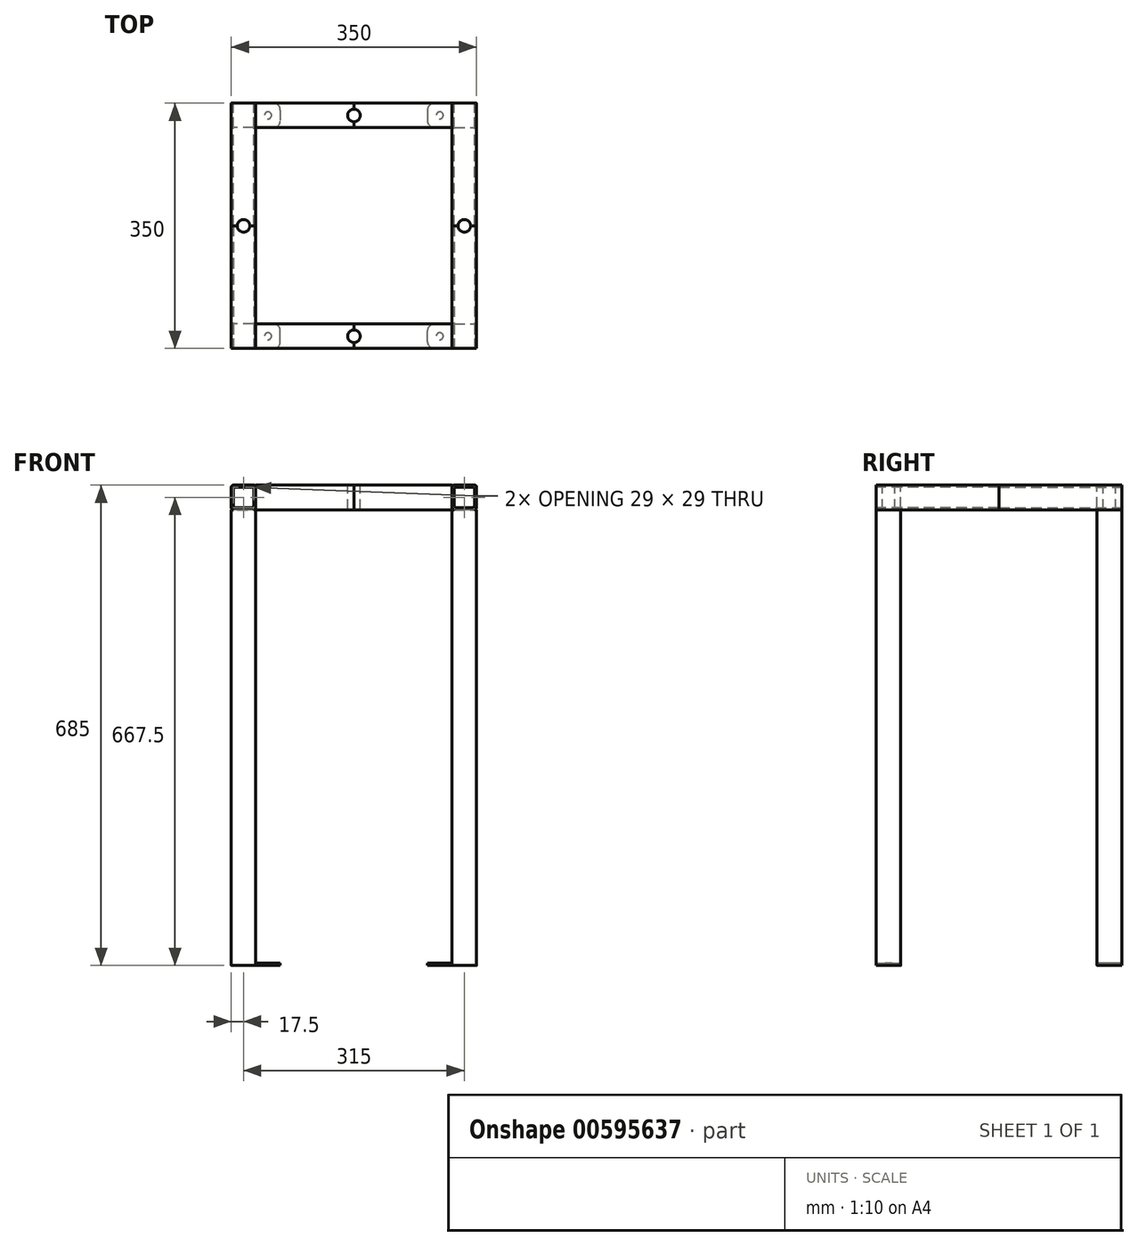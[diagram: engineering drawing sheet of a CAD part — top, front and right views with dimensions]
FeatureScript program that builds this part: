
annotation { "Feature Type Name" : "Feature", "Feature Type Description" : "" }
export const myFeature = defineFeature(function(context is Context, id is Id, definition is map)
    precondition{}
    {
        {
            var Q0;
            Q0=qCreatedBy(makeId("Top.planeOp"),FACE);
            var sketch = newSketch(context, id + "F0", { "sketchPlane" : qUnion([Q0])});
            skLineSegment(sketch, "E0.bottom", {"start": v(3, 0) * mm, "end": v(32, 0) * mm});
            skLineSegment(sketch, "E0.top", {"start": v(3, 35) * mm, "end": v(32, 35) * mm});
            skLineSegment(sketch, "E0.left", {"start": v(0, 3) * mm, "end": v(0, 32) * mm});
            skLineSegment(sketch, "E0.right", {"start": v(35, 3) * mm, "end": v(35, 32) * mm});
            skPoint(sketch, "E1.visualSharp", {"position": v(0, 35) * mm});
            skArc(sketch, "E1.filletArc", {"start": v(3, 35) * mm, "mid": v(0.88, 34.12) * mm, "end": v(0, 32) * mm});
            skPoint(sketch, "E2.visualSharp", {"position": v(35, 35) * mm});
            skArc(sketch, "E2.filletArc", {"start": v(35, 32) * mm, "mid": v(34.12, 34.12) * mm, "end": v(32, 35) * mm});
            skPoint(sketch, "E3.visualSharp", {"position": v(35, 0) * mm});
            skArc(sketch, "E3.filletArc", {"start": v(32, 0) * mm, "mid": v(34.12, 0.88) * mm, "end": v(35, 3) * mm});
            skPoint(sketch, "E4.visualSharp", {"position": v(0, 0) * mm});
            skArc(sketch, "E4.filletArc", {"start": v(0, 3) * mm, "mid": v(0.88, 0.88) * mm, "end": v(3, 0) * mm});
            skSolve(sketch);
        }
        {
            var Q0;
            Q0=makeQuery(id+"F0.imprint","IMPRINT",FACE,{"disambiguationData":[TD([[makeQuery(id+"F0.imprint","IMPRINT",EDGE,{"derivedFrom":sQuery(id+"F0.wireOp",EDGE,"E0.bottom")}),1.0]])]});
            extrude(context, id + "F1", {"entities" : qUnion([Q0]), "depth" : 650 * mm, "offsetDistance" : 25 * mm});
        }
        {
            var Q0;
            Q0=qCreatedBy(makeId("Right.planeOp"),FACE);
            var sketch = newSketch(context, id + "F2", { "sketchPlane" : qUnion([Q0])});
            skLineSegment(sketch, "E5.bottom", {"start": v(0, 0) * mm, "end": v(35, 0) * mm});
            skLineSegment(sketch, "E5.top", {"start": v(0, 3) * mm, "end": v(35, 3) * mm});
            skLineSegment(sketch, "E5.left", {"start": v(0, 0) * mm, "end": v(0, 3) * mm});
            skLineSegment(sketch, "E5.right", {"start": v(35, 0) * mm, "end": v(35, 3) * mm});
            skSolve(sketch);
        }
        {
            var Q0;
            Q0=makeQuery(id+"F2.imprint","IMPRINT",FACE,{"disambiguationData":[TD([[makeQuery(id+"F2.imprint","IMPRINT",EDGE,{"derivedFrom":sQuery(id+"F2.wireOp",EDGE,"E5.bottom")}),1.0]])]});
            extrude(context, id + "F3", {"entities" : qUnion([Q0]), "operationType" : NewBodyOperationType.ADD, "oppositeDirection" : true, "depth" : 35 * mm, "offsetDistance" : 25 * mm});
        }
        {
            var Q0;
            Q0=makeQuery(id+"F3.opExtrude","CAP_EDGE",EDGE,{"disambiguationData":[OSD([sQuery(id+"F2.wireOp",EDGE,"E5.left")])],"isStart":false});
            var Q1;
            Q1=makeQuery(id+"F3.opExtrude","CAP_EDGE",EDGE,{"disambiguationData":[OSD([sQuery(id+"F2.wireOp",EDGE,"E5.right")])],"isStart":false});
            fillet(context, id + "F4", {"entities" : qUnion([Q0, Q1]), "radius" : 10 * mm, "tangentPropagation" : true, "allowEdgeOverflow" : false});
        }
        {
            var Q0;
            Q0=makeQuery(id+"F3.opExtrude","SWEPT_FACE",FACE,{"disambiguationData":[OSD([sQuery(id+"F2.wireOp",EDGE,"E5.top")])]});
            var sketch = newSketch(context, id + "F5", { "sketchPlane" : qUnion([Q0])});
            skPoint(sketch, "E6", {"position": v(-17.5, 17.5) * mm});
            skPoint(sketch, "E6.positionSnap0", {"position": v(-35, 17.5) * mm});
            skSolve(sketch);
        }
        {
            var Q0;
            Q0=sQuery(id+"F5.wireOp",VERTEX,"E6");
            var Q1;
            Q1=makeQuery(id+"F1.opExtrude","SWEPT_BODY",BODY,{"disambiguationData":[OSD([sQuery(id+"F0.wireOp",EDGE,"E0.bottom"),sQuery(id+"F0.wireOp",EDGE,"E0.top"),sQuery(id+"F0.wireOp",EDGE,"E0.left"),sQuery(id+"F0.wireOp",EDGE,"E0.right"),sQuery(id+"F0.wireOp",EDGE,"E1.filletArc"),sQuery(id+"F0.wireOp",EDGE,"E2.filletArc"),sQuery(id+"F0.wireOp",EDGE,"E3.filletArc"),sQuery(id+"F0.wireOp",EDGE,"E4.filletArc")])]});
            hole(context, id + "F6", {"style" : HoleStyle.SIMPLE, "endStyle" : HoleEndStyle.BLIND, "holeDiameter" : 10 * mm, "majorDiameter" : 5 * mm, "holeDepth" : 3 * mm, "isTappedThrough" : true, "tappedDepth" : 12 * mm, "tapClearance" : 3, "startFromSketch" : true, "locations" : qUnion([Q0]), "scope" : qUnion([Q1])});
        }
        {
            var Q0;
            Q0=makeQuery(id+"F1.opExtrude","SWEPT_FACE",FACE,{"disambiguationData":[OSD([sQuery(id+"F0.wireOp",EDGE,"E0.bottom")])]});
            cPlane(context, id + "F7", {"entities" : qUnion([Q0]), "cplaneType" : CPlaneType.OFFSET, "offset" : 0 * mm, "width" : 150 * mm, "height" : 150 * mm});
        }
        {
            var Q0;
            Q0=qCreatedBy(id+"F7.planeOp",FACE);
            var sketch = newSketch(context, id + "F8", { "sketchPlane" : qUnion([Q0])});
            skLineSegment(sketch, "E7.bottom", {"start": v(3, 650) * mm, "end": v(32, 650) * mm});
            skLineSegment(sketch, "E7.top", {"start": v(3, 685) * mm, "end": v(32, 685) * mm});
            skLineSegment(sketch, "E7.left", {"start": v(0, 653) * mm, "end": v(0, 682) * mm});
            skLineSegment(sketch, "E7.right", {"start": v(35, 653) * mm, "end": v(35, 682) * mm});
            skPoint(sketch, "E8.visualSharp", {"position": v(0, 685) * mm});
            skArc(sketch, "E8.filletArc", {"start": v(3, 685) * mm, "mid": v(0.88, 684.12) * mm, "end": v(0, 682) * mm});
            skPoint(sketch, "E9.visualSharp", {"position": v(35, 685) * mm});
            skArc(sketch, "E9.filletArc", {"start": v(35, 682) * mm, "mid": v(34.12, 684.12) * mm, "end": v(32, 685) * mm});
            skPoint(sketch, "E10.visualSharp", {"position": v(35, 650) * mm});
            skArc(sketch, "E10.filletArc", {"start": v(32, 650) * mm, "mid": v(34.12, 650.88) * mm, "end": v(35, 653) * mm});
            skPoint(sketch, "E11.visualSharp", {"position": v(0, 650) * mm});
            skArc(sketch, "E11.filletArc", {"start": v(0, 653) * mm, "mid": v(0.88, 650.88) * mm, "end": v(3, 650) * mm});
            skLineSegment(sketch, "E12.bottom", {"start": v(6, 682) * mm, "end": v(29, 682) * mm});
            skLineSegment(sketch, "E12.top", {"start": v(6, 653) * mm, "end": v(29, 653) * mm});
            skLineSegment(sketch, "E12.left", {"start": v(3, 679) * mm, "end": v(3, 656) * mm});
            skLineSegment(sketch, "E12.right", {"start": v(32, 679) * mm, "end": v(32, 656) * mm});
            skArc(sketch, "E13.filletArc", {"start": v(6, 682) * mm, "mid": v(3.88, 681.12) * mm, "end": v(3, 679) * mm});
            skArc(sketch, "E14.filletArc", {"start": v(32, 679) * mm, "mid": v(31.12, 681.12) * mm, "end": v(29, 682) * mm});
            skArc(sketch, "E15.filletArc", {"start": v(29, 653) * mm, "mid": v(31.12, 653.88) * mm, "end": v(32, 656) * mm});
            skArc(sketch, "E16.filletArc", {"start": v(3, 656) * mm, "mid": v(3.88, 653.88) * mm, "end": v(6, 653) * mm});
            skSolve(sketch);
        }
        {
            var Q0;
            Q0=makeQuery(id+"F8.imprint","IMPRINT",FACE,{"disambiguationData":[TD([[makeQuery(id+"F8.imprint","IMPRINT",EDGE,{"derivedFrom":sQuery(id+"F8.wireOp",EDGE,"E7.bottom")}),1.0]])]});
            extrude(context, id + "F9", {"entities" : qUnion([Q0]), "operationType" : NewBodyOperationType.ADD, "oppositeDirection" : true, "depth" : 175 * mm, "offsetDistance" : 25 * mm});
        }
        {
            var Q0;
            Q0=qCreatedBy(makeId("Right.planeOp"),FACE);
            var sketch = newSketch(context, id + "F10", { "sketchPlane" : qUnion([Q0])});
            skLineSegment(sketch, "E17.bottom", {"start": v(32, 650) * mm, "end": v(3, 650) * mm});
            skLineSegment(sketch, "E17.top", {"start": v(32, 685) * mm, "end": v(3, 685) * mm});
            skLineSegment(sketch, "E17.left", {"start": v(35, 653) * mm, "end": v(35, 682) * mm});
            skLineSegment(sketch, "E17.right", {"start": v(0, 653) * mm, "end": v(0, 682) * mm});
            skPoint(sketch, "E18.visualSharp", {"position": v(35, 685) * mm});
            skArc(sketch, "E18.filletArc", {"start": v(35, 682) * mm, "mid": v(34.12, 684.12) * mm, "end": v(32, 685) * mm});
            skPoint(sketch, "E19.visualSharp", {"position": v(0, 685) * mm});
            skArc(sketch, "E19.filletArc", {"start": v(3, 685) * mm, "mid": v(0.88, 684.12) * mm, "end": v(0, 682) * mm});
            skPoint(sketch, "E20.visualSharp", {"position": v(0, 650) * mm});
            skArc(sketch, "E20.filletArc", {"start": v(0, 653) * mm, "mid": v(0.88, 650.88) * mm, "end": v(3, 650) * mm});
            skPoint(sketch, "E21.visualSharp", {"position": v(35, 650) * mm});
            skArc(sketch, "E21.filletArc", {"start": v(32, 650) * mm, "mid": v(34.12, 650.88) * mm, "end": v(35, 653) * mm});
            skSolve(sketch);
        }
        {
            var Q0;
            Q0=makeQuery(id+"F10.imprint","IMPRINT",FACE,{"disambiguationData":[TD([[makeQuery(id+"F10.imprint","IMPRINT",EDGE,{"derivedFrom":sQuery(id+"F10.wireOp",EDGE,"E17.bottom")}),-1.0]])]});
            extrude(context, id + "F11", {"entities" : qUnion([Q0]), "oppositeDirection" : true, "depth" : 140 * mm, "offsetDistance" : 25 * mm});
        }
        {
            var Q0;
            Q0=makeQuery(id+"F11.opExtrude","CAP_FACE",FACE,{"disambiguationData":[OSD([sQuery(id+"F10.wireOp",EDGE,"E17.bottom"),sQuery(id+"F10.wireOp",EDGE,"E17.top"),sQuery(id+"F10.wireOp",EDGE,"E17.left"),sQuery(id+"F10.wireOp",EDGE,"E17.right"),sQuery(id+"F10.wireOp",EDGE,"E18.filletArc"),sQuery(id+"F10.wireOp",EDGE,"E19.filletArc"),sQuery(id+"F10.wireOp",EDGE,"E20.filletArc"),sQuery(id+"F10.wireOp",EDGE,"E21.filletArc")])],"isStart":false});
            cPlane(context, id + "F12", {"entities" : qUnion([Q0]), "cplaneType" : CPlaneType.OFFSET, "offset" : 0 * mm, "width" : 150 * mm, "height" : 150 * mm});
        }
        {
            var Q0;
            Q0=makeQuery(id+"F11.opExtrude","SWEPT_BODY",BODY,{"disambiguationData":[OSD([sQuery(id+"F10.wireOp",EDGE,"E17.bottom"),sQuery(id+"F10.wireOp",EDGE,"E17.top"),sQuery(id+"F10.wireOp",EDGE,"E17.left"),sQuery(id+"F10.wireOp",EDGE,"E17.right"),sQuery(id+"F10.wireOp",EDGE,"E18.filletArc"),sQuery(id+"F10.wireOp",EDGE,"E19.filletArc"),sQuery(id+"F10.wireOp",EDGE,"E20.filletArc"),sQuery(id+"F10.wireOp",EDGE,"E21.filletArc")])]});
            var Q1;
            Q1=makeQuery(id+"F1.opExtrude","SWEPT_BODY",BODY,{"disambiguationData":[OSD([sQuery(id+"F0.wireOp",EDGE,"E0.bottom"),sQuery(id+"F0.wireOp",EDGE,"E0.top"),sQuery(id+"F0.wireOp",EDGE,"E0.left"),sQuery(id+"F0.wireOp",EDGE,"E0.right"),sQuery(id+"F0.wireOp",EDGE,"E1.filletArc"),sQuery(id+"F0.wireOp",EDGE,"E2.filletArc"),sQuery(id+"F0.wireOp",EDGE,"E3.filletArc"),sQuery(id+"F0.wireOp",EDGE,"E4.filletArc")])]});
            var Q2;
            Q2=qCreatedBy(id+"F12.planeOp",FACE);
            mirror(context, id + "F13", {"entities" : qUnion([Q0, Q1]), "mirrorPlane" : qUnion([Q2])});
        }
        {
            var Q0;
            Q0=makeQuery(id+"F9.opExtrude","CAP_FACE",FACE,{"disambiguationData":[OSD([sQuery(id+"F8.wireOp",EDGE,"E7.bottom"),sQuery(id+"F8.wireOp",EDGE,"E7.top"),sQuery(id+"F8.wireOp",EDGE,"E7.left"),sQuery(id+"F8.wireOp",EDGE,"E7.right"),sQuery(id+"F8.wireOp",EDGE,"E8.filletArc"),sQuery(id+"F8.wireOp",EDGE,"E9.filletArc"),sQuery(id+"F8.wireOp",EDGE,"E10.filletArc"),sQuery(id+"F8.wireOp",EDGE,"E11.filletArc"),sQuery(id+"F8.wireOp",EDGE,"E12.bottom"),sQuery(id+"F8.wireOp",EDGE,"E12.top"),sQuery(id+"F8.wireOp",EDGE,"E12.left"),sQuery(id+"F8.wireOp",EDGE,"E12.right"),sQuery(id+"F8.wireOp",EDGE,"E13.filletArc"),sQuery(id+"F8.wireOp",EDGE,"E14.filletArc"),sQuery(id+"F8.wireOp",EDGE,"E15.filletArc"),sQuery(id+"F8.wireOp",EDGE,"E16.filletArc")])],"isStart":false});
            cPlane(context, id + "F14", {"entities" : qUnion([Q0]), "cplaneType" : CPlaneType.OFFSET, "offset" : 0 * mm, "width" : 150 * mm, "height" : 150 * mm});
        }
        {
            var Q0;
            Q0=makeQuery(id+"F1.opExtrude","SWEPT_BODY",BODY,{"disambiguationData":[OSD([sQuery(id+"F0.wireOp",EDGE,"E0.bottom"),sQuery(id+"F0.wireOp",EDGE,"E0.top"),sQuery(id+"F0.wireOp",EDGE,"E0.left"),sQuery(id+"F0.wireOp",EDGE,"E0.right"),sQuery(id+"F0.wireOp",EDGE,"E1.filletArc"),sQuery(id+"F0.wireOp",EDGE,"E2.filletArc"),sQuery(id+"F0.wireOp",EDGE,"E3.filletArc"),sQuery(id+"F0.wireOp",EDGE,"E4.filletArc")])]});
            var Q1;
            Q1=makeQuery(id+"F11.opExtrude","SWEPT_BODY",BODY,{"disambiguationData":[OSD([sQuery(id+"F10.wireOp",EDGE,"E17.bottom"),sQuery(id+"F10.wireOp",EDGE,"E17.top"),sQuery(id+"F10.wireOp",EDGE,"E17.left"),sQuery(id+"F10.wireOp",EDGE,"E17.right"),sQuery(id+"F10.wireOp",EDGE,"E18.filletArc"),sQuery(id+"F10.wireOp",EDGE,"E19.filletArc"),sQuery(id+"F10.wireOp",EDGE,"E20.filletArc"),sQuery(id+"F10.wireOp",EDGE,"E21.filletArc")])]});
            var Q2;
            Q2=makeQuery(id+"F13.opPattern","COPY",BODY,{"derivedFrom":makeQuery(id+"F11.opExtrude","SWEPT_BODY",BODY,{"disambiguationData":[OSD([sQuery(id+"F10.wireOp",EDGE,"E17.bottom"),sQuery(id+"F10.wireOp",EDGE,"E17.top"),sQuery(id+"F10.wireOp",EDGE,"E17.left"),sQuery(id+"F10.wireOp",EDGE,"E17.right"),sQuery(id+"F10.wireOp",EDGE,"E18.filletArc"),sQuery(id+"F10.wireOp",EDGE,"E19.filletArc"),sQuery(id+"F10.wireOp",EDGE,"E20.filletArc"),sQuery(id+"F10.wireOp",EDGE,"E21.filletArc")])]}),"instanceName":"1"});
            var Q3;
            Q3=makeQuery(id+"F13.opPattern","COPY",BODY,{"derivedFrom":makeQuery(id+"F1.opExtrude","SWEPT_BODY",BODY,{"disambiguationData":[OSD([sQuery(id+"F0.wireOp",EDGE,"E0.bottom"),sQuery(id+"F0.wireOp",EDGE,"E0.top"),sQuery(id+"F0.wireOp",EDGE,"E0.left"),sQuery(id+"F0.wireOp",EDGE,"E0.right"),sQuery(id+"F0.wireOp",EDGE,"E1.filletArc"),sQuery(id+"F0.wireOp",EDGE,"E2.filletArc"),sQuery(id+"F0.wireOp",EDGE,"E3.filletArc"),sQuery(id+"F0.wireOp",EDGE,"E4.filletArc")])]}),"instanceName":"1"});
            var Q4;
            Q4=qCreatedBy(id+"F14.planeOp",FACE);
            mirror(context, id + "F15", {"entities" : qUnion([Q0, Q1, Q2, Q3]), "mirrorPlane" : qUnion([Q4])});
        }
        {
            var Q0;
            Q0=makeQuery(id+"F11.opExtrude","SWEPT_FACE",FACE,{"disambiguationData":[OSD([sQuery(id+"F10.wireOp",EDGE,"E17.top")])]});
            cPlane(context, id + "F16", {"entities" : qUnion([Q0]), "cplaneType" : CPlaneType.OFFSET, "offset" : 0 * mm, "width" : 150 * mm, "height" : 150 * mm});
        }
        {
            var Q0;
            Q0=qCreatedBy(id+"F16.planeOp",FACE);
            var sketch = newSketch(context, id + "F17", { "sketchPlane" : qUnion([Q0])});
            skPoint(sketch, "E22", {"position": v(-297.5, 175) * mm});
            skPoint(sketch, "E23", {"position": v(-140, 332.5) * mm});
            skPoint(sketch, "E24", {"position": v(17.5, 175) * mm});
            skPoint(sketch, "E25", {"position": v(-140, 17.5) * mm});
            skSolve(sketch);
        }
        {
            var Q0;
            Q0=sQuery(id+"F17.wireOp",VERTEX,"E22");
            var Q1;
            Q1=sQuery(id+"F17.wireOp",VERTEX,"E23");
            var Q2;
            Q2=sQuery(id+"F17.wireOp",VERTEX,"E24");
            var Q3;
            Q3=sQuery(id+"F17.wireOp",VERTEX,"E25");
            var Q4;
            Q4=makeQuery(id+"F1.opExtrude","SWEPT_BODY",BODY,{"disambiguationData":[OSD([sQuery(id+"F0.wireOp",EDGE,"E0.bottom"),sQuery(id+"F0.wireOp",EDGE,"E0.top"),sQuery(id+"F0.wireOp",EDGE,"E0.left"),sQuery(id+"F0.wireOp",EDGE,"E0.right"),sQuery(id+"F0.wireOp",EDGE,"E1.filletArc"),sQuery(id+"F0.wireOp",EDGE,"E2.filletArc"),sQuery(id+"F0.wireOp",EDGE,"E3.filletArc"),sQuery(id+"F0.wireOp",EDGE,"E4.filletArc")])]});
            var Q5;
            Q5=makeQuery(id+"F11.opExtrude","SWEPT_BODY",BODY,{"disambiguationData":[OSD([sQuery(id+"F10.wireOp",EDGE,"E17.bottom"),sQuery(id+"F10.wireOp",EDGE,"E17.top"),sQuery(id+"F10.wireOp",EDGE,"E17.left"),sQuery(id+"F10.wireOp",EDGE,"E17.right"),sQuery(id+"F10.wireOp",EDGE,"E18.filletArc"),sQuery(id+"F10.wireOp",EDGE,"E19.filletArc"),sQuery(id+"F10.wireOp",EDGE,"E20.filletArc"),sQuery(id+"F10.wireOp",EDGE,"E21.filletArc")])]});
            var Q6;
            Q6=makeQuery(id+"F13.opPattern","COPY",BODY,{"derivedFrom":makeQuery(id+"F11.opExtrude","SWEPT_BODY",BODY,{"disambiguationData":[OSD([sQuery(id+"F10.wireOp",EDGE,"E17.bottom"),sQuery(id+"F10.wireOp",EDGE,"E17.top"),sQuery(id+"F10.wireOp",EDGE,"E17.left"),sQuery(id+"F10.wireOp",EDGE,"E17.right"),sQuery(id+"F10.wireOp",EDGE,"E18.filletArc"),sQuery(id+"F10.wireOp",EDGE,"E19.filletArc"),sQuery(id+"F10.wireOp",EDGE,"E20.filletArc"),sQuery(id+"F10.wireOp",EDGE,"E21.filletArc")])]}),"instanceName":"1"});
            var Q7;
            Q7=makeQuery(id+"F13.opPattern","COPY",BODY,{"derivedFrom":makeQuery(id+"F1.opExtrude","SWEPT_BODY",BODY,{"disambiguationData":[OSD([sQuery(id+"F0.wireOp",EDGE,"E0.bottom"),sQuery(id+"F0.wireOp",EDGE,"E0.top"),sQuery(id+"F0.wireOp",EDGE,"E0.left"),sQuery(id+"F0.wireOp",EDGE,"E0.right"),sQuery(id+"F0.wireOp",EDGE,"E1.filletArc"),sQuery(id+"F0.wireOp",EDGE,"E2.filletArc"),sQuery(id+"F0.wireOp",EDGE,"E3.filletArc"),sQuery(id+"F0.wireOp",EDGE,"E4.filletArc")])]}),"instanceName":"1"});
            var Q8;
            Q8=makeQuery(id+"F15.opPattern","COPY",BODY,{"derivedFrom":makeQuery(id+"F13.opPattern","COPY",BODY,{"derivedFrom":makeQuery(id+"F1.opExtrude","SWEPT_BODY",BODY,{"disambiguationData":[OSD([sQuery(id+"F0.wireOp",EDGE,"E0.bottom"),sQuery(id+"F0.wireOp",EDGE,"E0.top"),sQuery(id+"F0.wireOp",EDGE,"E0.left"),sQuery(id+"F0.wireOp",EDGE,"E0.right"),sQuery(id+"F0.wireOp",EDGE,"E1.filletArc"),sQuery(id+"F0.wireOp",EDGE,"E2.filletArc"),sQuery(id+"F0.wireOp",EDGE,"E3.filletArc"),sQuery(id+"F0.wireOp",EDGE,"E4.filletArc")])]}),"instanceName":"1"}),"instanceName":"1"});
            var Q9;
            Q9=makeQuery(id+"F15.opPattern","COPY",BODY,{"derivedFrom":makeQuery(id+"F11.opExtrude","SWEPT_BODY",BODY,{"disambiguationData":[OSD([sQuery(id+"F10.wireOp",EDGE,"E17.bottom"),sQuery(id+"F10.wireOp",EDGE,"E17.top"),sQuery(id+"F10.wireOp",EDGE,"E17.left"),sQuery(id+"F10.wireOp",EDGE,"E17.right"),sQuery(id+"F10.wireOp",EDGE,"E18.filletArc"),sQuery(id+"F10.wireOp",EDGE,"E19.filletArc"),sQuery(id+"F10.wireOp",EDGE,"E20.filletArc"),sQuery(id+"F10.wireOp",EDGE,"E21.filletArc")])]}),"instanceName":"1"});
            var Q10;
            Q10=makeQuery(id+"F15.opPattern","COPY",BODY,{"derivedFrom":makeQuery(id+"F13.opPattern","COPY",BODY,{"derivedFrom":makeQuery(id+"F11.opExtrude","SWEPT_BODY",BODY,{"disambiguationData":[OSD([sQuery(id+"F10.wireOp",EDGE,"E17.bottom"),sQuery(id+"F10.wireOp",EDGE,"E17.top"),sQuery(id+"F10.wireOp",EDGE,"E17.left"),sQuery(id+"F10.wireOp",EDGE,"E17.right"),sQuery(id+"F10.wireOp",EDGE,"E18.filletArc"),sQuery(id+"F10.wireOp",EDGE,"E19.filletArc"),sQuery(id+"F10.wireOp",EDGE,"E20.filletArc"),sQuery(id+"F10.wireOp",EDGE,"E21.filletArc")])]}),"instanceName":"1"}),"instanceName":"1"});
            var Q11;
            Q11=makeQuery(id+"F15.opPattern","COPY",BODY,{"derivedFrom":makeQuery(id+"F1.opExtrude","SWEPT_BODY",BODY,{"disambiguationData":[OSD([sQuery(id+"F0.wireOp",EDGE,"E0.bottom"),sQuery(id+"F0.wireOp",EDGE,"E0.top"),sQuery(id+"F0.wireOp",EDGE,"E0.left"),sQuery(id+"F0.wireOp",EDGE,"E0.right"),sQuery(id+"F0.wireOp",EDGE,"E1.filletArc"),sQuery(id+"F0.wireOp",EDGE,"E2.filletArc"),sQuery(id+"F0.wireOp",EDGE,"E3.filletArc"),sQuery(id+"F0.wireOp",EDGE,"E4.filletArc")])]}),"instanceName":"1"});
            hole(context, id + "F18", {"style" : HoleStyle.SIMPLE, "endStyle" : HoleEndStyle.THROUGH, "holeDiameter" : 18 * mm, "majorDiameter" : 5 * mm, "isTappedThrough" : true, "tappedDepth" : 12 * mm, "tapClearance" : 3, "startFromSketch" : true, "locations" : qUnion([Q0, Q1, Q2, Q3]), "scope" : qUnion([Q4, Q5, Q6, Q7, Q8, Q9, Q10, Q11])});
        }
    });
